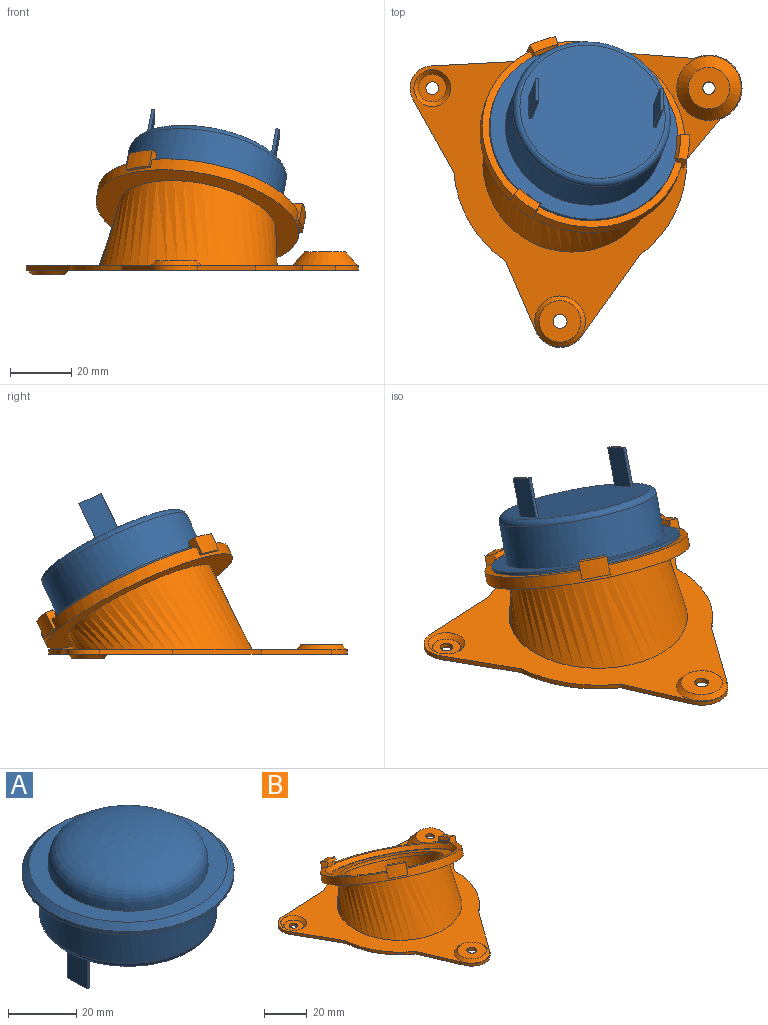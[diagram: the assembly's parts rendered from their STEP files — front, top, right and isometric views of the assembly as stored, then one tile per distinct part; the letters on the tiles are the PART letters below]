
ASSEMBLY  parts=2 mates=1
PART A: 18 faces, bbox 156.2x156.2x126 mm
  f0: cylinder r=31.1mm len=62.2mm, axis (0,0,-1), area 195.4mm2, adj f2,f3
  f1: plane 152.2x152.2mm, normal (0,0,1), area 925.4mm2, adj f3,f17
  f2: plane 62.2x62.2mm, normal (0,0,-1), area 914.9mm2, adj f0,f4
  f3: cone r=29.1mm half-angle=45deg, axis (0,0,-1), area 534.9mm2, adj f0,f1
  f4: cylinder r=26mm len=52mm, axis (0,0,1), area 2287.1mm2, adj f2,f6
  f5: plane 48x48mm, normal (0,0,-1), area 1793.6mm2, adj f6,f7,f8,f9,f10,f12,f13,f14
  f6: torus R=24mm, axis (0,0,-1), area 498.9mm2, adj f4,f5
  f7: plane 13x1mm, normal (0,1,0), area 13mm2, adj f5,f8,f10,f11
  f8: plane 13x8mm, normal (1,0,0), area 104mm2, adj f5,f7,f9,f11
  f9: plane 13x1mm, normal (0,-1,0), area 13mm2, adj f5,f8,f10,f11
  f10: plane 13x8mm, normal (-1,0,0), area 104mm2, adj f5,f7,f9,f11
  f11: plane 8x1mm, normal (0,0,-1), area 8mm2, adj f7,f8,f9,f10
  f12: plane 13x8mm, normal (1,0,0), area 104mm2, adj f5,f13,f15,f16
  f13: plane 13x1mm, normal (0,-1,0), area 13mm2, adj f5,f12,f14,f16
  f14: plane 13x8mm, normal (-1,0,0), area 104mm2, adj f5,f13,f15,f16
  f15: plane 13x1mm, normal (0,1,0), area 13mm2, adj f5,f12,f14,f16
  f16: plane 8x1mm, normal (0,0,-1), area 8mm2, adj f12,f13,f14,f15
  f17: revolved ~47x23.5mm, area 0mm2, adj f1
PART B: 71 faces, bbox 108x101.1x40.7 mm
  f0: cylinder r=33.5mm len=66.69mm, axis (-0.17,-0.43,-0.89), area 760.1mm2, adj f47,f48,f50,f51,f53,f54,f57,f60
  f1: plane 108x97.23mm, normal (0,0,1), area 2836.4mm2, adj f5,f6,f7,f8,f9,f10,f11,f12
  f2: plane 108x97.23mm, normal (0,0,-1), area 3175.1mm2, adj f5,f6,f7,f8,f9,f10,f11,f12
  f3: cylinder r=2mm len=4mm, axis (0,0,1), area 18.8mm2, adj f27,f29
  f4: cylinder r=2.26mm len=4.53mm, axis (0,0,1), area 21.3mm2, adj f18,f24
  f5: plane 41.6x3.23mm, normal (0.08,1,0), area 62.6mm2, adj f1,f2,f6,f17
  f6: cylinder r=37.25mm len=15.37mm, axis (0,0,1), area 24.1mm2, adj f1,f2,f5,f7
  f7: plane 28.66x1.5mm, normal (-0.05,1,0), area 43.1mm2, adj f1,f2,f6,f8
  f8: cylinder r=7.25mm len=10.79mm, axis (0,0,1), area 22.1mm2, adj f1,f2,f7,f9
  f9: plane 23.81x13.35mm, normal (-0.87,-0.49,0), area 41mm2, adj f1,f2,f8,f10
  f10: cylinder r=38.55mm len=28.91mm, axis (0,0,1), area 51.9mm2, adj f1,f2,f9,f11
  f11: plane 22.96x9.9mm, normal (-0.92,-0.4,0), area 37.5mm2, adj f1,f2,f10,f12
  f12: cylinder r=8.5mm len=14.71mm, axis (0,0,1), area 26.9mm2, adj f1,f2,f11,f13
  f13: plane 26.4x18.95mm, normal (0.81,-0.58,0), area 48.7mm2, adj f1,f2,f12,f14
  f14: cylinder r=37.25mm len=31.23mm, axis (0,0,1), area 54.3mm2, adj f1,f2,f13,f15
  f15: plane 13.05x10.9mm, normal (0.77,-0.64,0), area 25.5mm2, adj f1,f2,f14,f17
  f16: cylinder r=2.06mm len=4.13mm, axis (0,0,1), area 19.4mm2, adj f20,f21
  f17: cylinder r=10.75mm len=20.88mm, axis (0,0,1), area 52.5mm2, adj f1,f2,f5,f15
  f18: plane 13.5x13.5mm, normal (0,0,1), area 127mm2, adj f4,f19
  f19: cone r=6.75mm half-angle=45deg, axis (0,0,-1), area 100mm2, adj f1,f18
  f20: plane 10.5x10.5mm, normal (0,0,-1), area 73.2mm2, adj f16,f23
  f21: plane 9x9mm, normal (0,0,1), area 50.2mm2, adj f16,f22
  f22: cone r=4.5mm half-angle=45deg, axis (0,0,1), area 70mm2, adj f1,f21
  f23: cone r=5.25mm half-angle=45deg, axis (0,0,1), area 80mm2, adj f2,f20
  f24: plane 12.5x12.5mm, normal (0,0,-1), area 106.6mm2, adj f4,f25
  f25: cone r=6.25mm half-angle=45deg, axis (0,0,-1), area 93.3mm2, adj f2,f24
  f26: cylinder r=10.5mm len=21mm, axis (0,0,-1), area 2mm2, adj f1,f31
  f27: plane 13.5x13.5mm, normal (0,0,1), area 130.6mm2, adj f3,f31
  f28: cylinder r=9.25mm len=18.5mm, axis (0,0,-1), area 1.8mm2, adj f2,f30
  f29: plane 11x11mm, normal (0,0,-1), area 82.5mm2, adj f3,f30
  f30: cone r=5.5mm half-angle=40deg, axis (0,0,-1), area 270.3mm2, adj f28,f29
  f31: cone r=6.75mm half-angle=40deg, axis (0,0,-1), area 316.2mm2, adj f26,f27
  f32: cylinder r=27.5mm len=55mm, axis (0,0,1), area 259.2mm2, adj f2,f64
  f33: bspline ~59.96x57.95mm, area 2969.1mm2, adj f1,f57
  f34: plane 1.27x1.15mm, normal (-0.23,-0.86,0.46), area 0.7mm2, adj f35,f36,f37,f63
  f35: plane 7.59x3.85mm, normal (-0.17,-0.43,-0.89), area 7.6mm2, adj f34,f37,f47,f63
  f36: cone r=30.55mm half-angle=35deg, axis (0.17,0.43,0.89), area 13.8mm2, adj f34,f37,f47,f63
  f37: torus R=30.59mm, axis (0.17,0.43,0.89), area 0.9mm2, adj f34,f35,f36,f47
  f38: plane 1.65x0.66mm, normal (-0.72,0.67,-0.19), area 0.7mm2, adj f39,f40,f41,f62
  f39: plane 7.22x5.52mm, normal (-0.17,-0.43,-0.89), area 7.6mm2, adj f38,f41,f50,f62
  f40: cone r=30.55mm half-angle=35deg, axis (0.17,0.43,0.89), area 13.8mm2, adj f38,f41,f50,f62
  f41: torus R=30.59mm, axis (0.17,0.43,0.89), area 0.9mm2, adj f38,f39,f40,f50
  f42: plane 1.44x1.27mm, normal (0.94,0.19,-0.27), area 0.7mm2, adj f43,f44,f45,f61
  f43: plane 7.88x3.3mm, normal (-0.17,-0.43,-0.89), area 7.6mm2, adj f42,f45,f54,f61
  f44: cone r=30.55mm half-angle=35deg, axis (0.17,0.43,0.89), area 13.8mm2, adj f42,f45,f54,f61
  f45: torus R=30.59mm, axis (0.17,0.43,0.89), area 0.9mm2, adj f42,f43,f44,f54
  f46: plane 8.42x4.33mm, normal (0.17,0.43,0.89), area 26.9mm2, adj f47,f48,f63,f69
  f47: plane 5.84x4.14mm, normal (-0.04,0.9,-0.43), area 12.7mm2, adj f0,f35,f36,f37,f46,f60,f63,f69
  f48: plane 5.47x3.42mm, normal (-0.23,-0.86,0.46), area 12mm2, adj f0,f46,f60,f63,f69,f70
  f49: plane 8.85x7.28mm, normal (0.17,0.43,0.89), area 26.9mm2, adj f50,f51,f62,f67
  f50: plane 5.78x4.96mm, normal (0.87,-0.49,0.07), area 12.7mm2, adj f0,f39,f40,f41,f49,f60,f62,f67
  f51: plane 5.74x4.38mm, normal (-0.71,0.67,-0.19), area 12mm2, adj f0,f49,f60,f62,f67,f68
  f52: plane 9.22x5.23mm, normal (0.17,0.43,0.89), area 26.9mm2, adj f53,f54,f61,f65
  f53: plane 6.44x3.94mm, normal (0.94,0.18,-0.27), area 12mm2, adj f0,f52,f60,f61,f65,f66
  f54: plane 6.18x3.8mm, normal (-0.83,-0.41,0.36), area 12.7mm2, adj f0,f43,f44,f45,f52,f60,f61,f65
  f55: cone r=29mm half-angle=45deg, axis (0.17,0.43,0.89), area 560.7mm2, adj f56,f60
  f56: cylinder r=29mm len=57.2mm, axis (-0.17,-0.43,-0.89), area 72.9mm2, adj f55,f58
  f57: plane 66x60.54mm, normal (-0.17,-0.43,-0.89), area 1419.6mm2, adj f0,f33
  f58: plane 57.13x52.41mm, normal (0.17,0.43,0.89), area 756.3mm2, adj f56,f59
  f59: cylinder r=24.5mm len=48.52mm, axis (-0.17,-0.43,-0.89), area 230.9mm2, adj f58,f64
  f60: plane 65.97x60.54mm, normal (0.17,0.43,0.89), area 434.1mm2, adj f0,f47,f48,f50,f51,f53,f54,f55
  f61: cylinder r=31.5mm len=8.17mm, axis (-0.17,-0.43,-0.89), area 13.5mm2, adj f42,f43,f44,f52,f53,f54,f60
  f62: cylinder r=31.5mm len=7.34mm, axis (-0.17,-0.43,-0.89), area 13.5mm2, adj f38,f39,f40,f49,f50,f51,f60
  f63: cylinder r=31.5mm len=8.86mm, axis (-0.17,-0.43,-0.89), area 13.5mm2, adj f34,f35,f36,f46,f47,f48,f60
  f64: bspline ~57.21x54.96mm, area 2822.7mm2, adj f32,f59
  f65: cylinder r=34.5mm len=9.42mm, axis (-0.17,-0.43,-0.89), area 56.2mm2, adj f52,f53,f54,f66
  f66: plane 8.66x3.63mm, normal (-0.17,-0.43,-0.89), area 9.2mm2, adj f0,f53,f54,f65
  f67: cylinder r=34.5mm len=8.5mm, axis (-0.17,-0.43,-0.89), area 56.2mm2, adj f49,f50,f51,f68
  f68: plane 7.93x6.08mm, normal (-0.17,-0.43,-0.89), area 9.2mm2, adj f0,f50,f51,f67
  f69: cylinder r=34.5mm len=10.87mm, axis (-0.17,-0.43,-0.89), area 56.2mm2, adj f46,f47,f48,f70
  f70: plane 8.34x4.23mm, normal (-0.17,-0.43,-0.89), area 9.2mm2, adj f0,f47,f48,f69
PLACE A rot(axis=(1,-0.02,-0.09),154.3deg) t=(27.22,-0.15,25.99)mm
PLACE B t=(1.14,2.83,5.85)mm
MATE fastened A.f0 <-> B.f55  axis (-0.17,-0.43,-0.89) through (26.7,-1.43,23.33)mm
